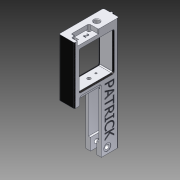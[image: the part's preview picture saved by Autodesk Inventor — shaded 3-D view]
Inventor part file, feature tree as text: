
AUTODESK INVENTOR PART (.ipt)
format: ipt  version: 2012 (Build 160160000, 160)  size: 899,072 bytes
history: native  units: mm
features: extrude x21, fillet x18, sketch x11, chamfer x8, emboss x3
ambient origin geometry x8: Origin, YZ Plane, XZ Plane, XY Plane, X Axis, Y Axis, Z Axis, Center Point
bodies: Solid1 (feature_tree)
feature tree (61):
  sketch  "Sketch2"  dims[d0=72.5mm d1=33.0mm]
  extrude  "Extrusion1"  Depth=33.0mm
  extrude  "Extrusion2"  Depth=16.0mm
  extrude  "Extrusion3"  Depth=12.0mm
  extrude  "Extrusion4"  Depth=117.0mm
  extrude  "Extrusion16"  Depth=8.8mm
  chamfer  "Chamfer1"  Distance=30.0mm
  chamfer  "Chamfer2"  Distance=4.0mm
  extrude  "Extrusion5"  Depth=24.0mm TaperAngle=0.0deg
  fillet  "Fillet1"  Radius=4.0mm
  fillet  "Fillet2"  Radius=5.0mm
  fillet  "Fillet3"  Radius=5.0mm
  fillet  "Fillet4"  Radius=20.0mm
  fillet  "Fillet5"  Radius=2.0mm
  fillet  "Fillet6"  Radius=2.0mm
  sketch  "Sketch4"  dims[d4=10.0mm d5=12.0mm]
  extrude  "Extrusion7"  Depth=3.0mm
  extrude  "Extrusion8"  Depth=10.0mm
  chamfer  "Chamfer3"  Distance=1.8mm
  extrude  "Extrusion9"  Depth=10.0mm
  chamfer  "Chamfer4"  Distance=15.0mm
  extrude  "Extrusion6"  Depth=60.0mm TaperAngle=0.0deg
  chamfer  "Chamfer5"  Distance=2.0mm
  chamfer  "Chamfer6"  Distance=1.0mm
  extrude  "Extrusion10"  Depth=6.4mm
  chamfer  "Chamfer7"  Distance=40.0mm
  fillet  "Fillet7"  Radius=100.0mm
  extrude  "Extrusion11"  Depth=1.0mm TaperAngle=45.0deg
  fillet  "Fillet8"  Radius=14.0mm
  extrude  "Extrusion12"  Depth=1.0mm TaperAngle=0.0deg
  extrude  "Extrusion13"  Depth=2.4mm TaperAngle=45.0deg
  extrude  "Extrusion14"  Depth=16.0mm
  fillet  "Fillet9"  Radius=15.0mm
  fillet  "Fillet10"  Radius=1.0mm
  extrude  "Extrusion15"  Depth=1.0mm TaperAngle=45.0deg
  emboss  "Emboss1"
  fillet  "Fillet11"  Radius=1.0mm
  fillet  "Fillet12"  Radius=4.0mm
  emboss  "Emboss2"
  sketch  "Sketch10"  dims[d15=12.0mm]
  extrude  "Extrusion17"  Depth=2.0mm
  chamfer  "Chamfer8"  Distance=32.0mm
  extrude  "Extrusion18"  Depth=6.0mm
  fillet  "Fillet14"  Radius=12.2mm
  fillet  "Fillet15"  Radius=14.0mm
  fillet  "Fillet16"  Radius=6.0mm
  extrude  "Extrusion19"  Depth=2.0mm
  extrude  "Extrusion20"  Depth=6.0mm
  fillet  "Fillet17"  Radius=44.0mm
  fillet  "Fillet18"  Radius=50.0mm
  fillet  "Fillet19"  Radius=6.0mm
  emboss  "Emboss4"
  extrude  "Extrusion21"  Depth=10.0mm
  sketch  "Sketch3"  dims[d2=33.0mm d3=16.0mm]
  sketch  "Sketch5"  dims[d6=10.0mm d7=117.0mm]
  sketch  "Sketch6"  dims[d8=9.0mm d9=8.8mm]
  sketch  "Sketch7"  dims[d10=26.0mm]
  sketch  "Sketch8"  dims[d11=32.0mm]
  sketch  "Sketch9"  dims[d14=30.0mm]
  sketch  "Sketch12"  dims[d16=4.0mm]
  sketch  "Sketch13"  dims[d17=12.0mm d18=30.0mm d19=0.0mm d20=4.0mm d21=0.0mm d22=24.0mm d23=0.0mm d24=4.0mm d25=0.0mm d26=5.0mm d27=4.0mm d28=45.0deg d29=5.0mm d30=4.0mm d31=45.0deg d32=20.0mm d33=0.0mm d34=2.0mm d35=2.0mm d36=3.0mm d37=10.0mm d38=1.8mm d39=10.0mm d40=15.0mm d41=60.0mm d42=0.0mm d43=2.0mm d44=1.0mm d45=6.4mm d46=40.0mm d47=78.0mm d48=0.0mm d49=0.0mm d52=100.0mm d53=0.0mm d54=1.0mm d55=7.0mm d56=45.0deg d57=14.0mm d58=1.0mm d59=0.0mm d60=2.4mm d61=1.0mm d62=45.0deg d63=16.0mm d64=15.0mm d65=1.0mm d66=3.0mm d67=45.0deg d68=1.0mm d69=3.0mm d70=45.0deg d73=1.0mm d74=0.0mm d75=4.0mm d76=1.0mm d77=45.0deg d78=2.0mm d79=32.0mm d80=6.0mm d81=12.2mm d82=14.0mm d83=6.0mm d84=0.0mm d87=2.0mm d88=6.0mm d89=44.0mm d90=50.0mm d91=6.0mm d92=0.0mm d93=10.0mm d94=10.0mm d95=8.2mm d96=20.5mm d97=11.5mm d98=23.0mm d99=6.0mm d100=0.0mm d101=12.0mm d102=0.0mm d103=4.0mm d104=2.0mm d105=14.0mm d106=0.75mm d107=0.0mm d108=1.0mm d109=0.0mm d110=110.0mm d111=6.0mm d112=24.0mm d113=0.0mm d114=4.0mm d115=4.0mm d116=0.5mm d117=0.0mm d118=10.5mm d119=14.0mm d124=8.2mm d125=0.0mm d126=1.0mm d127=2.0mm d128=45.0deg d129=6.6mm d130=6.2mm d131=3.8mm d132=0.0mm d134=2.2mm d135=1.0mm d136=1.6mm d137=3.0mm d138=10.0mm d139=3.0mm d140=0.0mm d141=0.0mm d142=9.0mm d143=5.0mm d144=0.0mm d145=3.0mm d146=4.2mm d147=2.0mm d148=2.0mm d151=37.4mm d152=0.5mm d153=0.0mm d154=3.5mm d155=7.06mm d156=13.5mm d157=1.0mm d158=0.0mm d159=15.5mm d160=2.0mm]
